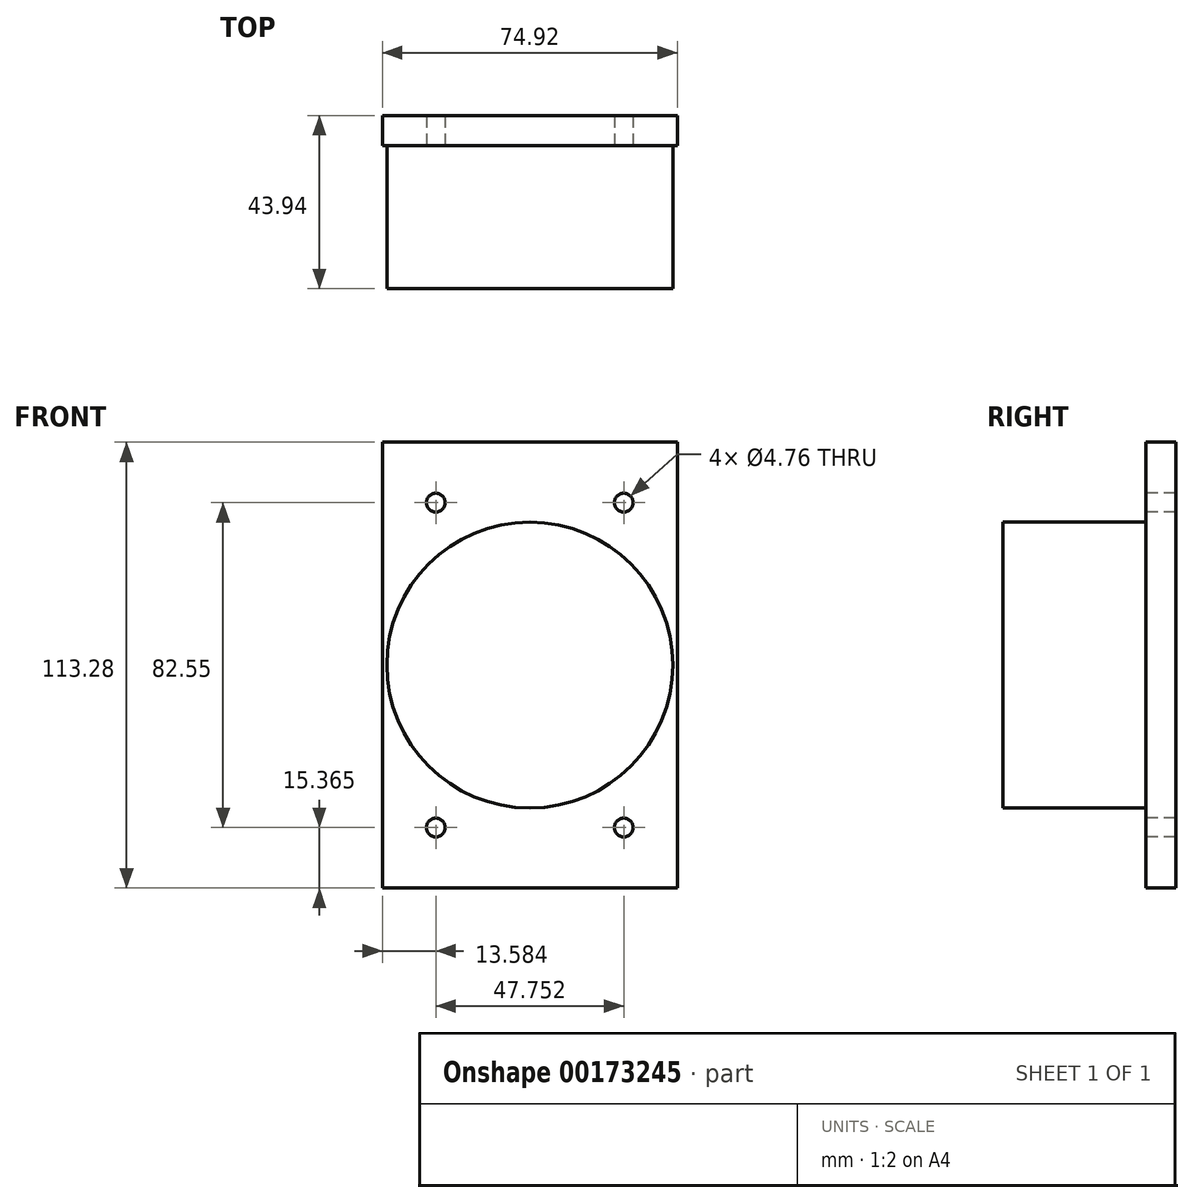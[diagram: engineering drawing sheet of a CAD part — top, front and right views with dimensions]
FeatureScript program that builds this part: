
annotation { "Feature Type Name" : "Feature", "Feature Type Description" : "" }
export const myFeature = defineFeature(function(context is Context, id is Id, definition is map)
    precondition{}
    {
        {
            var Q0;
            Q0=qCreatedBy(makeId("Front.planeOp"),FACE);
            var sketch = newSketch(context, id + "F0", { "sketchPlane" : qUnion([Q0])});
            skLineSegment(sketch, "E0.bottom", {"start": v(-37.46, 56.64) * mm, "end": v(37.47, 56.64) * mm});
            skLineSegment(sketch, "E0.top", {"start": v(-37.47, -56.64) * mm, "end": v(37.46, -56.64) * mm});
            skLineSegment(sketch, "E0.left", {"start": v(-37.46, 56.64) * mm, "end": v(-37.47, -56.64) * mm});
            skLineSegment(sketch, "E0.right", {"start": v(37.47, 56.64) * mm, "end": v(37.46, -56.64) * mm});
            skPoint(sketch, "E0.middle", {"position": v(0, 0) * mm});
            skSolve(sketch);
        }
        {
            var Q0;
            Q0 = qSketchRegion(id + "F0", true);
            extrude(context, id + "F1", {"entities" : qUnion([Q0]), "depth" : 7.62 * mm});
        }
        {
            var Q0;
            Q0=makeQuery(id+"F1.opExtrude","CAP_FACE",FACE,{"disambiguationData":[OSD([sQuery(id+"F0.wireOp",EDGE,"E0.bottom"),sQuery(id+"F0.wireOp",EDGE,"E0.top"),sQuery(id+"F0.wireOp",EDGE,"E0.left"),sQuery(id+"F0.wireOp",EDGE,"E0.right")])],"isStart":false});
            var sketch = newSketch(context, id + "F2", { "sketchPlane" : qUnion([Q0])});
            skLineSegment(sketch, "E1", {"start": v(0, 56.64) * mm, "end": v(0, -56.64) * mm});
            skLineSegment(sketch, "E2", {"start": v(-37.47, 0) * mm, "end": v(37.46, 0) * mm});
            skCircle(sketch, "E3", {"center": v(23.88, 41.27) * mm, "radius": 2.38 * mm});
            skCircle(sketch, "E4", {"center": v(-23.88, 41.27) * mm, "radius": 2.38 * mm});
            skCircle(sketch, "E5", {"center": v(-23.88, -41.28) * mm, "radius": 2.38 * mm});
            skCircle(sketch, "E6", {"center": v(23.88, -41.28) * mm, "radius": 2.38 * mm});
            skSolve(sketch);
        }
        {
            var Q0;
            Q0 = qSketchRegion(id + "F2", true);
            extrude(context, id + "F3", {"entities" : qUnion([Q0]), "operationType" : NewBodyOperationType.REMOVE, "endBound" : BoundingType.THROUGH_ALL, "oppositeDirection" : true, "depth" : 25.4 * mm});
        }
        {
            var Q0;
            Q0=makeQuery(id+"F1.opExtrude","CAP_FACE",FACE,{"disambiguationData":[OSD([sQuery(id+"F0.wireOp",EDGE,"E0.bottom"),sQuery(id+"F0.wireOp",EDGE,"E0.top"),sQuery(id+"F0.wireOp",EDGE,"E0.left"),sQuery(id+"F0.wireOp",EDGE,"E0.right")])],"isStart":false});
            var sketch = newSketch(context, id + "F4", { "sketchPlane" : qUnion([Q0])});
            skCircle(sketch, "E7", {"center": v(0, 0) * mm, "radius": 36.32 * mm});
            skSolve(sketch);
        }
        {
            var Q0;
            Q0 = qSketchRegion(id + "F4", true);
            extrude(context, id + "F5", {"entities" : qUnion([Q0]), "operationType" : NewBodyOperationType.ADD, "depth" : 36.32 * mm});
        }
    });
